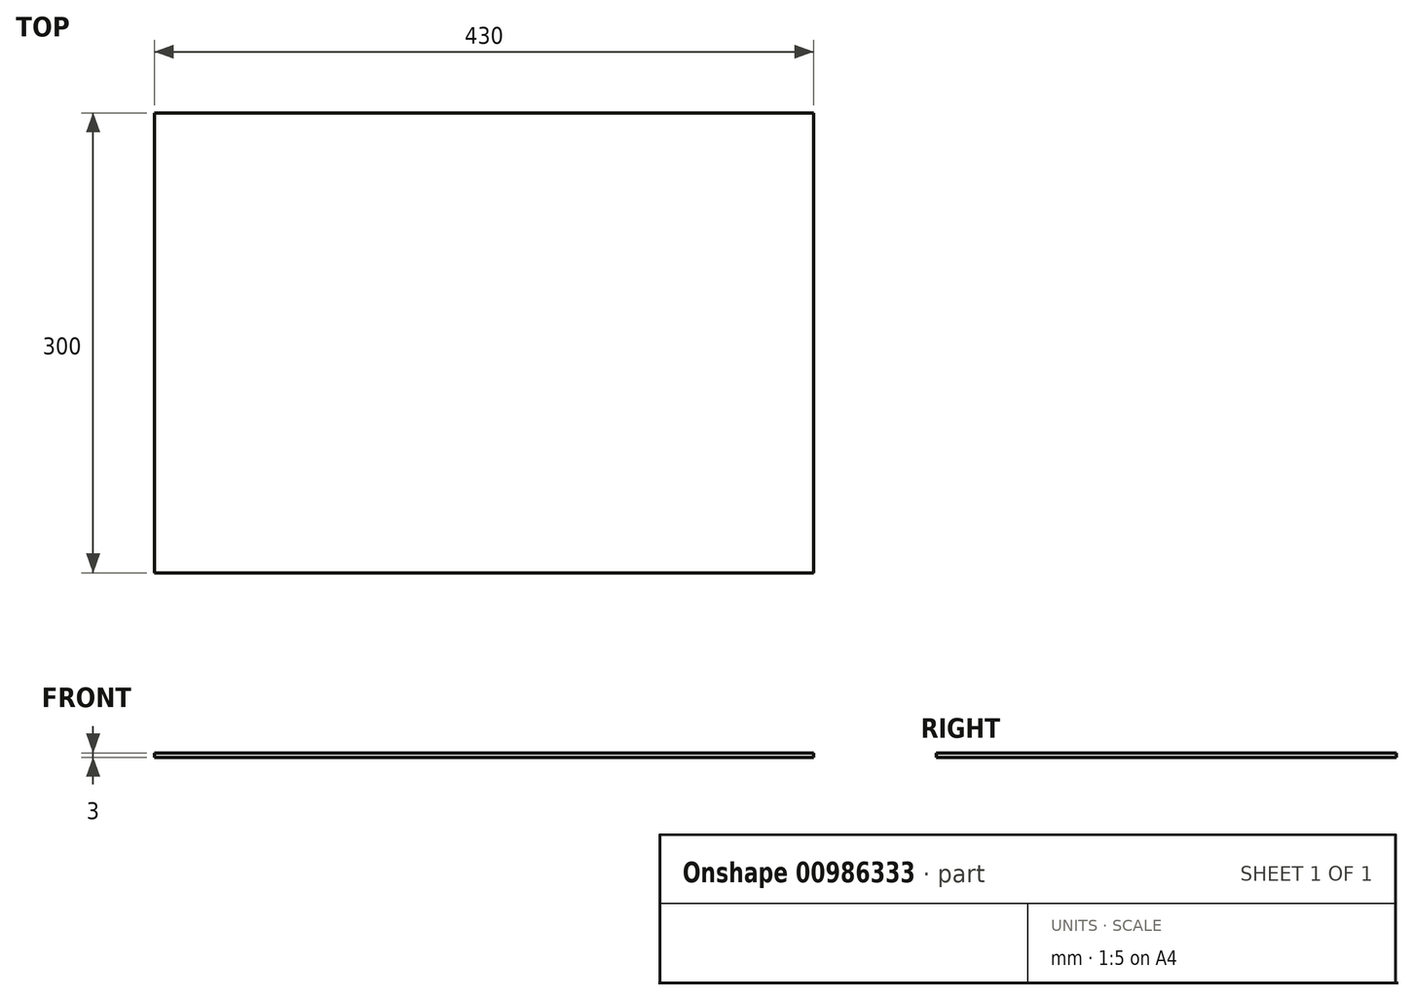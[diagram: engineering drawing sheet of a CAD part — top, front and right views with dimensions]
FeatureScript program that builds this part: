
annotation { "Feature Type Name" : "Feature", "Feature Type Description" : "" }
export const myFeature = defineFeature(function(context is Context, id is Id, definition is map)
    precondition{}
    {
        {
            var Q0;
            Q0=qCreatedBy(makeId("Top.planeOp"),FACE);
            var sketch = newSketch(context, id + "F0", { "sketchPlane" : qUnion([Q0])});
            skLineSegment(sketch, "E0.bottom", {"start": v(215, 150) * mm, "end": v(-215, 150) * mm});
            skLineSegment(sketch, "E0.top", {"start": v(215, -150) * mm, "end": v(-215, -150) * mm});
            skLineSegment(sketch, "E0.left", {"start": v(215, 150) * mm, "end": v(215, -150) * mm});
            skLineSegment(sketch, "E0.right", {"start": v(-215, 150) * mm, "end": v(-215, -150) * mm});
            skPoint(sketch, "E0.middle", {"position": v(0, 0) * mm});
            skSolve(sketch);
        }
        {
            var Q0;
            Q0 = qSketchRegion(id + "F0", true);
            extrude(context, id + "F1", {"entities" : qUnion([Q0]), "depth" : 3 * mm, "offsetDistance" : 25 * mm});
        }
    });
